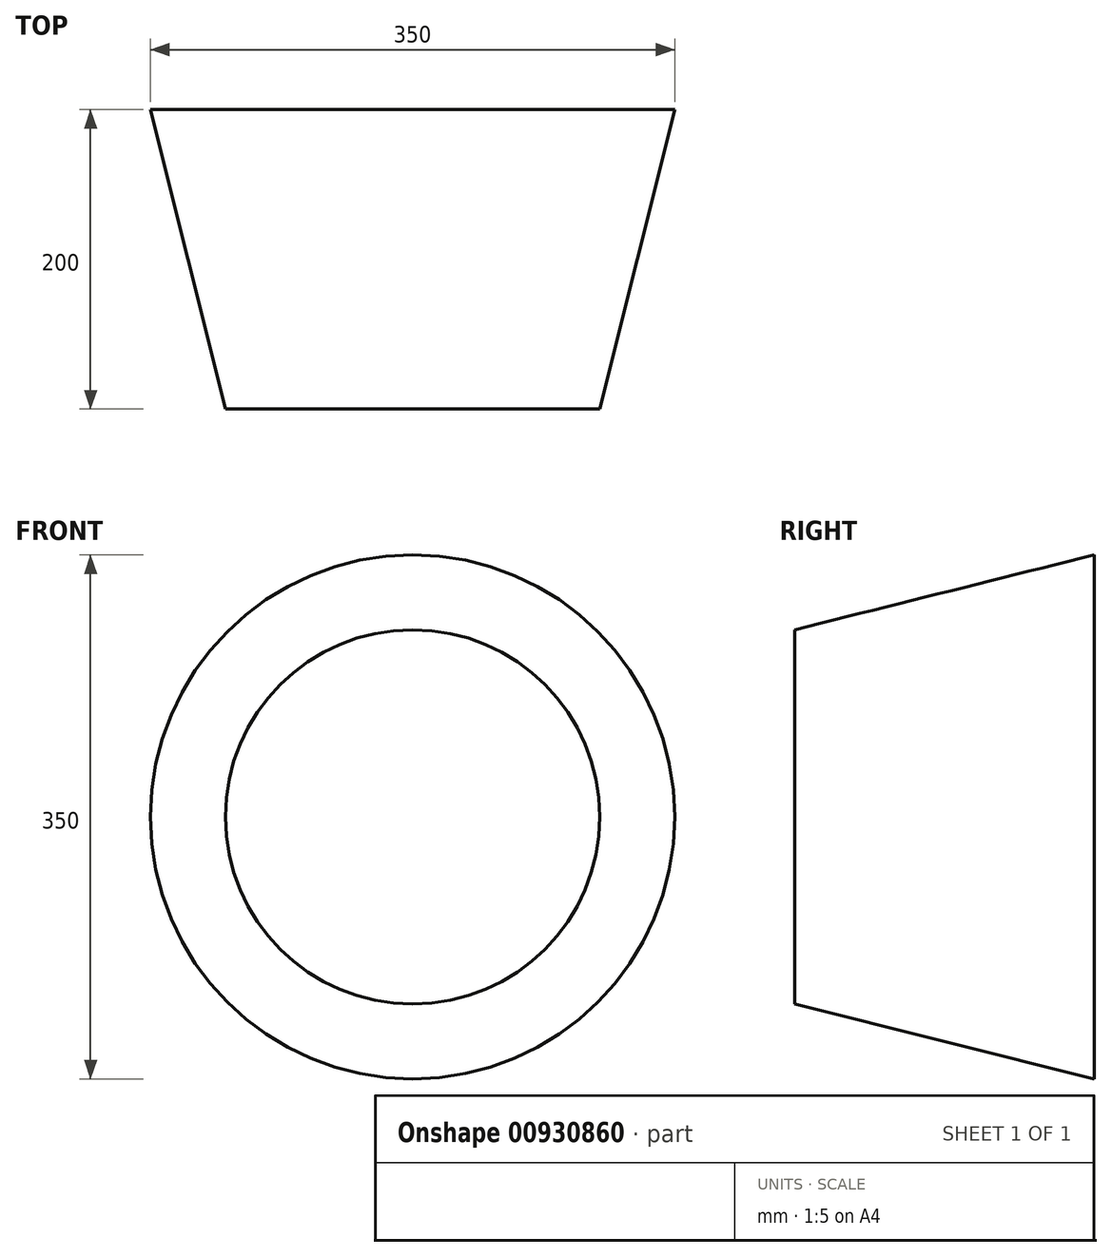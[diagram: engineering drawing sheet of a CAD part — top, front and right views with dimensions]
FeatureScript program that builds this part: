
annotation { "Feature Type Name" : "Feature", "Feature Type Description" : "" }
export const myFeature = defineFeature(function(context is Context, id is Id, definition is map)
    precondition{}
    {
        {
            var Q0;
            Q0=qCreatedBy(makeId("Top.planeOp"),FACE);
            var sketch = newSketch(context, id + "F0", { "sketchPlane" : qUnion([Q0])});
            skLineSegment(sketch, "E0", {"start": v(0, 0) * mm, "end": v(-125, 0) * mm});
            skLineSegment(sketch, "E1", {"start": v(-125, 0) * mm, "end": v(-175, 200) * mm});
            skLineSegment(sketch, "E2", {"start": v(-175, 200) * mm, "end": v(0, 200) * mm});
            skLineSegment(sketch, "E3", {"start": v(0, 200) * mm, "end": v(0, 0) * mm});
            skSolve(sketch);
        }
        {
            var Q0;
            Q0=makeQuery(id+"F0.imprint","IMPRINT",FACE,{"disambiguationData":[TD([[makeQuery(id+"F0.imprint","IMPRINT",EDGE,{"derivedFrom":sQuery(id+"F0.wireOp",EDGE,"E0")}),-1.0]])]});
            var Q1;
            Q1=sQuery(id+"F0.wireOp",EDGE,"E3");
            revolve(context, id + "F1", {"surfaceOperationType" : NewSurfaceOperationType.NEW, "entities" : qUnion([Q0]), "axis" : qUnion([Q1]), "revolveType" : RevolveType.FULL});
        }
    });
